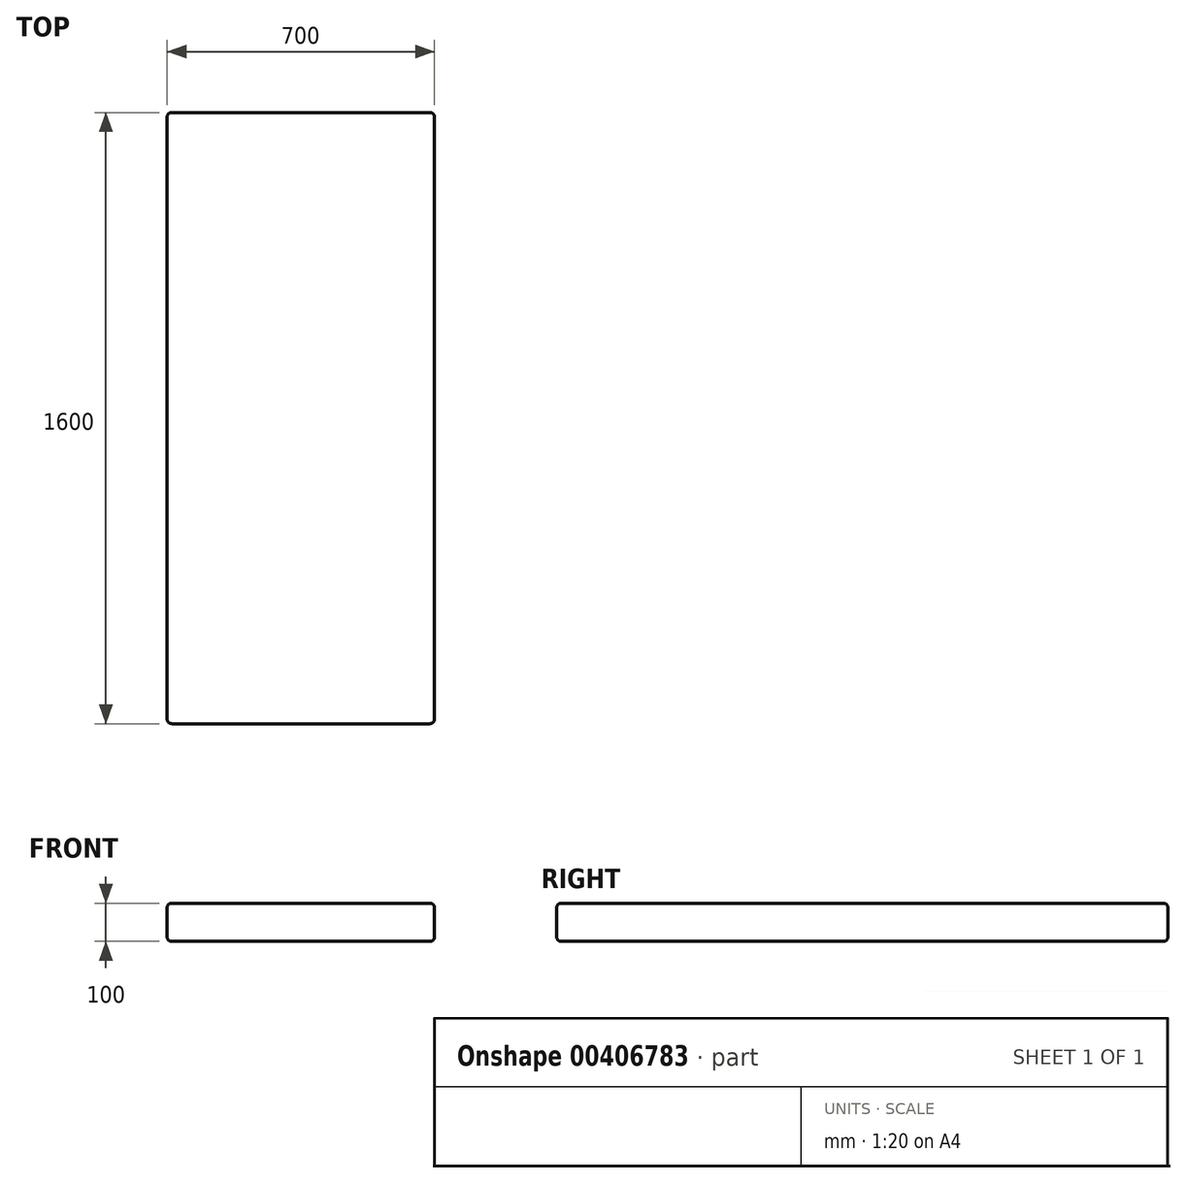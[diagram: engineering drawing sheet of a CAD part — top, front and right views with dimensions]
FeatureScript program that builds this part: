
annotation { "Feature Type Name" : "Feature", "Feature Type Description" : "" }
export const myFeature = defineFeature(function(context is Context, id is Id, definition is map)
    precondition{}
    {
        {
            var Q0;
            Q0=qCreatedBy(makeId("Top.planeOp"),FACE);
            var sketch = newSketch(context, id + "F0", { "sketchPlane" : qUnion([Q0])});
            skLineSegment(sketch, "E0.bottom", {"start": v(-350, 800) * mm, "end": v(350, 800) * mm});
            skLineSegment(sketch, "E0.top", {"start": v(-350, -800) * mm, "end": v(350, -800) * mm});
            skLineSegment(sketch, "E0.left", {"start": v(-350, 800) * mm, "end": v(-350, -800) * mm});
            skLineSegment(sketch, "E0.right", {"start": v(350, 800) * mm, "end": v(350, -800) * mm});
            skPoint(sketch, "E0.middle", {"position": v(0, 0) * mm});
            skSolve(sketch);
        }
        {
            var Q0;
            Q0 = qSketchRegion(id + "F0", true);
            extrude(context, id + "F1", {"entities" : qUnion([Q0]), "offsetDistance" : 25 * mm, "depth" : 100 * mm});
        }
        {
            var Q0;
            Q0=makeQuery(id+"F1.opExtrude","CAP_EDGE",EDGE,{"disambiguationData":[OSD([sQuery(id+"F0.wireOp",EDGE,"E0.top")])],"isStart":false});
            var Q1;
            Q1=makeQuery(id+"F1.opExtrude","CAP_EDGE",EDGE,{"disambiguationData":[OSD([sQuery(id+"F0.wireOp",EDGE,"E0.left")])],"isStart":false});
            var Q2;
            Q2=makeQuery(id+"F1.opExtrude","CAP_EDGE",EDGE,{"disambiguationData":[OSD([sQuery(id+"F0.wireOp",EDGE,"E0.right")])],"isStart":true});
            var Q3;
            Q3=makeQuery(id+"F1.opExtrude","CAP_EDGE",EDGE,{"disambiguationData":[OSD([sQuery(id+"F0.wireOp",EDGE,"E0.right")])],"isStart":false});
            var Q4;
            Q4=makeQuery(id+"F1.opExtrude","SWEPT_EDGE",EDGE,{"disambiguationData":[OSD([sQuery(id+"F0.wireOp",EDGE,"E0.top"),sQuery(id+"F0.wireOp",EDGE,"E0.right")])]});
            var Q5;
            Q5=makeQuery(id+"F1.opExtrude","SWEPT_EDGE",EDGE,{"disambiguationData":[OSD([sQuery(id+"F0.wireOp",EDGE,"E0.top"),sQuery(id+"F0.wireOp",EDGE,"E0.left")])]});
            var Q6;
            Q6=makeQuery(id+"F1.opExtrude","SWEPT_EDGE",EDGE,{"disambiguationData":[OSD([sQuery(id+"F0.wireOp",EDGE,"E0.bottom"),sQuery(id+"F0.wireOp",EDGE,"E0.right")])]});
            var Q7;
            Q7=makeQuery(id+"F1.opExtrude","SWEPT_EDGE",EDGE,{"disambiguationData":[OSD([sQuery(id+"F0.wireOp",EDGE,"E0.bottom"),sQuery(id+"F0.wireOp",EDGE,"E0.left")])]});
            var Q8;
            Q8=makeQuery(id+"F1.opExtrude","CAP_EDGE",EDGE,{"disambiguationData":[OSD([sQuery(id+"F0.wireOp",EDGE,"E0.bottom")])],"isStart":true});
            var Q9;
            Q9=makeQuery(id+"F1.opExtrude","CAP_EDGE",EDGE,{"disambiguationData":[OSD([sQuery(id+"F0.wireOp",EDGE,"E0.bottom")])],"isStart":false});
            var Q10;
            Q10=makeQuery(id+"F1.opExtrude","CAP_EDGE",EDGE,{"disambiguationData":[OSD([sQuery(id+"F0.wireOp",EDGE,"E0.top")])],"isStart":true});
            var Q11;
            Q11=makeQuery(id+"F1.opExtrude","CAP_EDGE",EDGE,{"disambiguationData":[OSD([sQuery(id+"F0.wireOp",EDGE,"E0.left")])],"isStart":true});
            fillet(context, id + "F2", {"entities" : qUnion([Q0, Q1, Q2, Q3, Q4, Q5, Q6, Q7, Q8, Q9, Q10, Q11]), "radius" : 12 * mm, "tangentPropagation" : true, "allowEdgeOverflow" : false});
        }
    });
